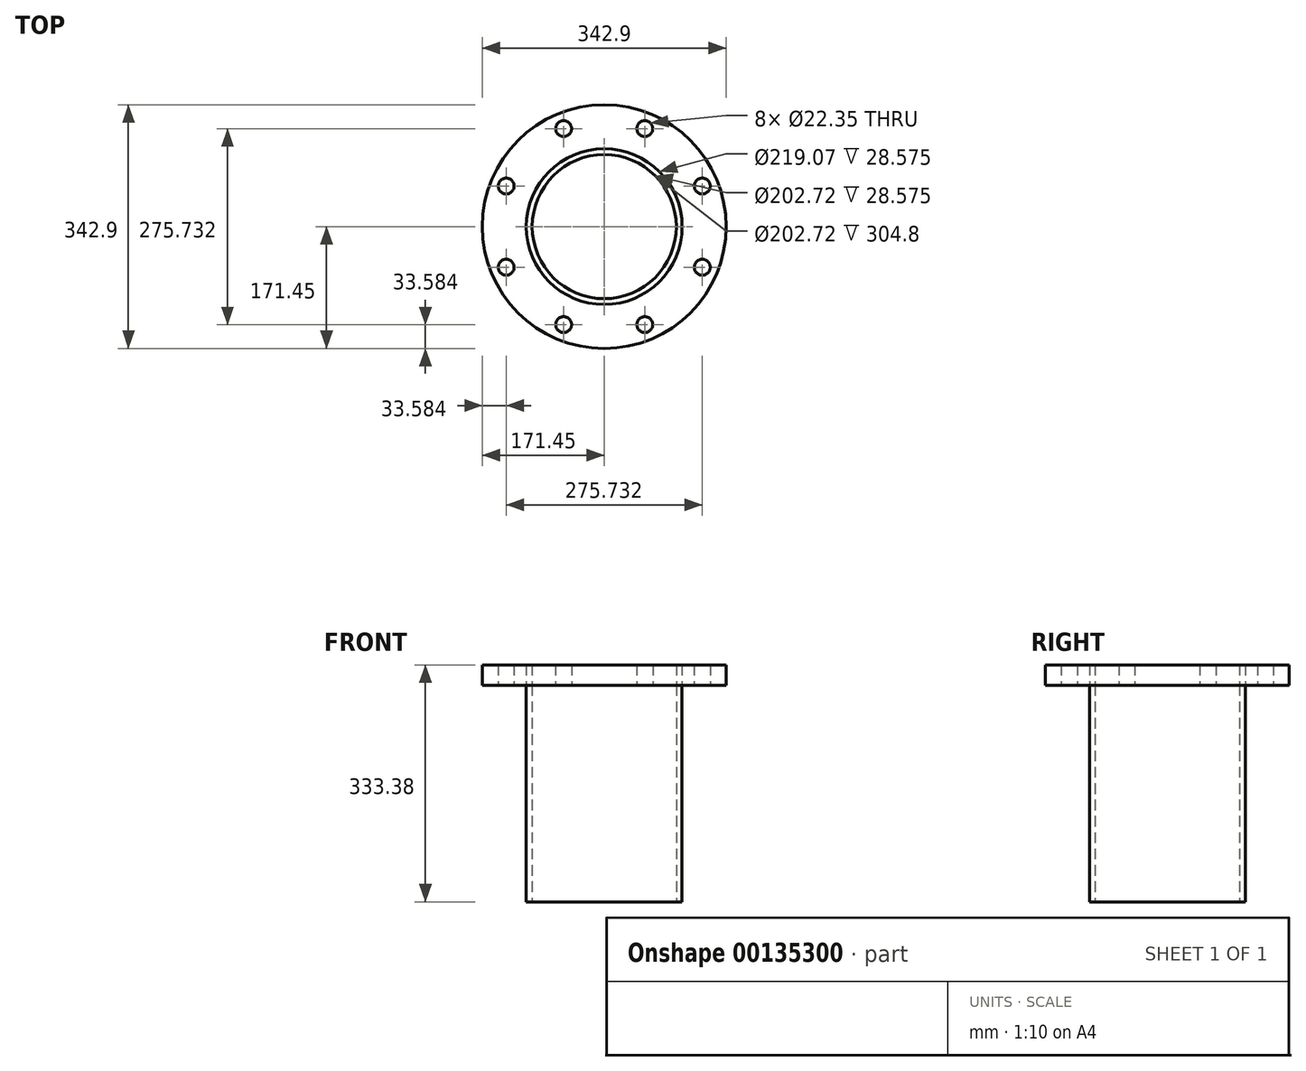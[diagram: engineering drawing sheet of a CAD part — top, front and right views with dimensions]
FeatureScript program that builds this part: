
annotation { "Feature Type Name" : "Feature", "Feature Type Description" : "" }
export const myFeature = defineFeature(function(context is Context, id is Id, definition is map)
    precondition{}
    {
        {
            var Q0;
            Q0=qCreatedBy(makeId("Top.planeOp"),FACE);
            var sketch = newSketch(context, id + "F0", { "sketchPlane" : qUnion([Q0])});
            skCircle(sketch, "E0", {"center": v(0, 0) * mm, "radius": 109.54 * mm});
            skCircle(sketch, "E1", {"center": v(0, 0) * mm, "radius": 101.36 * mm});
            skSolve(sketch);
        }
        {
            var Q0;
            Q0=makeQuery(id+"F0.imprint","IMPRINT",FACE,{"disambiguationData":[TD([[makeQuery(id+"F0.imprint","IMPRINT",EDGE,{"derivedFrom":sQuery(id+"F0.wireOp",EDGE,"E0")}),1.0]])]});
            extrude(context, id + "F1", {"entities" : qUnion([Q0]), "depth" : 304.8 * mm});
        }
        {
            var Q0;
            Q0=makeQuery(id+"F1.opExtrude","CAP_FACE",FACE,{"disambiguationData":[OSD([sQuery(id+"F0.wireOp",EDGE,"E0"),sQuery(id+"F0.wireOp",EDGE,"E1")])],"isStart":false});
            var sketch = newSketch(context, id + "F2", { "sketchPlane" : qUnion([Q0])});
            skCircle(sketch, "E2", {"center": v(0, 0) * mm, "radius": 149.23 * mm, "construction": true});
            skCircle(sketch, "E3", {"center": v(57.1, 137.87) * mm, "radius": 11.18 * mm});
            skCircle(sketch, "E4", {"center": v(0, 0) * mm, "radius": 171.45 * mm});
            skCircle(sketch, "E5.1.0", {"center": v(-57.1, 137.87) * mm, "radius": 11.18 * mm});
            skCircle(sketch, "E5.2.0", {"center": v(-137.87, 57.1) * mm, "radius": 11.18 * mm});
            skCircle(sketch, "E5.3.0", {"center": v(-137.87, -57.1) * mm, "radius": 11.18 * mm});
            skCircle(sketch, "E5.4.0", {"center": v(-57.1, -137.87) * mm, "radius": 11.18 * mm});
            skCircle(sketch, "E5.5.0", {"center": v(57.1, -137.87) * mm, "radius": 11.18 * mm});
            skCircle(sketch, "E5.6.0", {"center": v(137.87, -57.1) * mm, "radius": 11.18 * mm});
            skCircle(sketch, "E5.7.0", {"center": v(137.87, 57.1) * mm, "radius": 11.18 * mm});
            skLineSegment(sketch, "E6", {"start": v(-57.1, 137.87) * mm, "end": v(57.1, 137.87) * mm, "construction": true});
            skSolve(sketch);
        }
        {
            var Q0;
            Q0=makeQuery(id+"F2.imprint","IMPRINT",FACE,{"disambiguationData":[TD([[makeQuery(id+"F2.imprint","IMPRINT",EDGE,{"derivedFrom":sQuery(id+"F2.wireOp",EDGE,"zaJDvXjR-FGGZ-jiN2-OxFt-qx0oZYHT2mIo")}),1.0]])]});
            var Q1;
            Q1=makeQuery(id+"F2.imprint","IMPRINT",FACE,{"disambiguationData":[TD([[makeQuery(id+"F2.imprint","IMPRINT",EDGE,{"derivedFrom":sQuery(id+"F2.wireOp",EDGE,"E3")}),-1.0]])]});
            extrude(context, id + "F3", {"entities" : qUnion([Q0, Q1]), "depth" : 28.57 * mm});
        }
        {
            var Q0;
            Q0=makeQuery(id+"F1.opExtrude","CAP_FACE",FACE,{"disambiguationData":[OSD([sQuery(id+"F0.wireOp",EDGE,"E0"),sQuery(id+"F0.wireOp",EDGE,"E1")])],"isStart":false});
            extrude(context, id + "F4", {"entities" : qUnion([Q0]), "depth" : 28.57 * mm});
        }
    });
